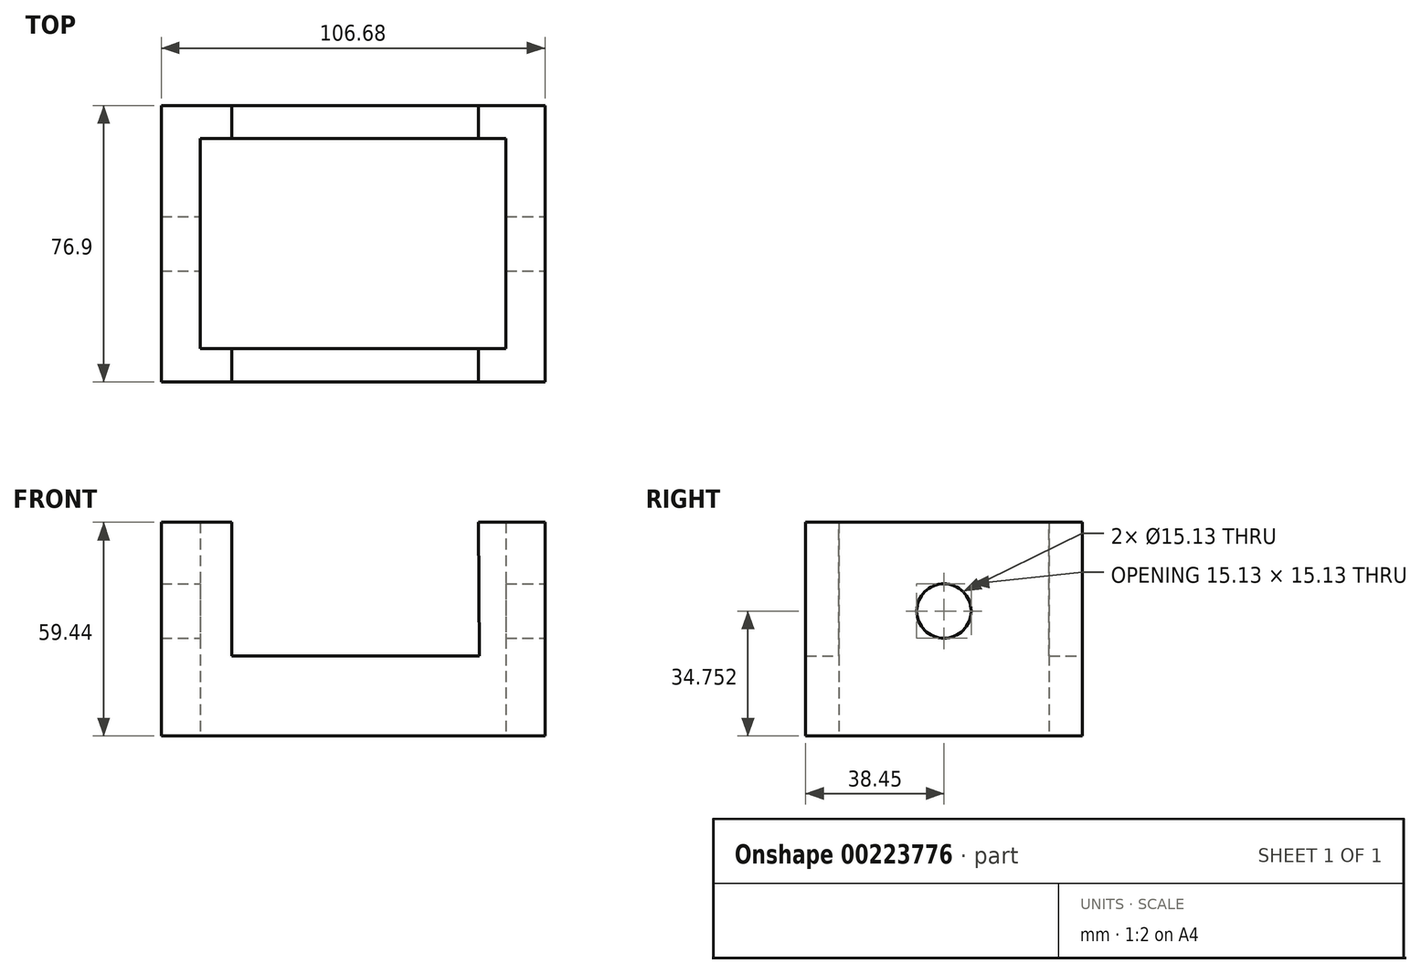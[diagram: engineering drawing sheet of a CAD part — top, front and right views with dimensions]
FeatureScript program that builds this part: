
annotation { "Feature Type Name" : "Feature", "Feature Type Description" : "" }
export const myFeature = defineFeature(function(context is Context, id is Id, definition is map)
    precondition{}
    {
        {
            var Q0;
            Q0=qCreatedBy(makeId("Top.planeOp"),FACE);
            var sketch = newSketch(context, id + "F0", { "sketchPlane" : qUnion([Q0])});
            skLineSegment(sketch, "E0.bottom", {"start": v(-53.34, 38.45) * mm, "end": v(53.34, 38.45) * mm});
            skLineSegment(sketch, "E0.top", {"start": v(-53.34, -38.45) * mm, "end": v(53.34, -38.45) * mm});
            skLineSegment(sketch, "E0.left", {"start": v(-53.34, 38.45) * mm, "end": v(-53.34, -38.45) * mm});
            skLineSegment(sketch, "E0.right", {"start": v(53.34, 38.45) * mm, "end": v(53.34, -38.45) * mm});
            skPoint(sketch, "E0.middle", {"position": v(0, 0) * mm});
            skSolve(sketch);
        }
        {
            var Q0;
            Q0 = qSketchRegion(id + "F0", true);
            extrude(context, id + "F1", {"entities" : qUnion([Q0]), "depth" : 59.44 * mm});
        }
        {
            var Q0;
            Q0=qCreatedBy(makeId("Top.planeOp"),FACE);
            var sketch = newSketch(context, id + "F2", { "sketchPlane" : qUnion([Q0])});
            skLineSegment(sketch, "E1.bottom", {"start": v(42.49, -29.21) * mm, "end": v(-42.49, -29.21) * mm});
            skLineSegment(sketch, "E1.top", {"start": v(42.49, 29.21) * mm, "end": v(-42.49, 29.21) * mm});
            skLineSegment(sketch, "E1.left", {"start": v(42.49, -29.21) * mm, "end": v(42.49, 29.21) * mm});
            skLineSegment(sketch, "E1.right", {"start": v(-42.49, -29.21) * mm, "end": v(-42.49, 29.21) * mm});
            skPoint(sketch, "E1.middle", {"position": v(0, 0) * mm});
            skSolve(sketch);
        }
        {
            var Q0;
            Q0 = qSketchRegion(id + "F2", true);
            extrude(context, id + "F3", {"entities" : qUnion([Q0]), "operationType" : NewBodyOperationType.REMOVE, "endBound" : BoundingType.THROUGH_ALL, "depth" : 85.1 * mm});
        }
        {
            var Q0;
            Q0=qCreatedBy(makeId("Front.planeOp"),FACE);
            var sketch = newSketch(context, id + "F4", { "sketchPlane" : qUnion([Q0])});
            skLineSegment(sketch, "E2", {"start": v(-33.71, 64.08) * mm, "end": v(-33.71, 22.28) * mm});
            skLineSegment(sketch, "E3", {"start": v(-33.71, 22.28) * mm, "end": v(35.1, 22.28) * mm});
            skLineSegment(sketch, "E4", {"start": v(35.1, 22.28) * mm, "end": v(34.87, 64.3) * mm});
            skLineSegment(sketch, "E5", {"start": v(-33.71, 64.08) * mm, "end": v(34.87, 64.3) * mm});
            skSolve(sketch);
        }
        {
            var Q0;
            Q0 = qSketchRegion(id + "F4", true);
            extrude(context, id + "F5", {"entities" : qUnion([Q0]), "operationType" : NewBodyOperationType.REMOVE, "depth" : 80.77 * mm, "hasSecondDirection" : true, "secondDirectionOppositeDirection" : true, "secondDirectionDepth" : 74.42 * mm});
        }
        {
            var Q0;
            Q0=qCreatedBy(makeId("Right.planeOp"),FACE);
            var sketch = newSketch(context, id + "F6", { "sketchPlane" : qUnion([Q0])});
            skCircle(sketch, "E6", {"center": v(0, 34.75) * mm, "radius": 7.56 * mm});
            skSolve(sketch);
        }
        {
            var Q0;
            Q0 = qSketchRegion(id + "F6", true);
            extrude(context, id + "F7", {"entities" : qUnion([Q0]), "operationType" : NewBodyOperationType.REMOVE, "oppositeDirection" : true, "depth" : 66.55 * mm, "hasSecondDirection" : true, "secondDirectionOppositeDirection" : false, "secondDirectionDepth" : 73.15 * mm});
        }
    });
